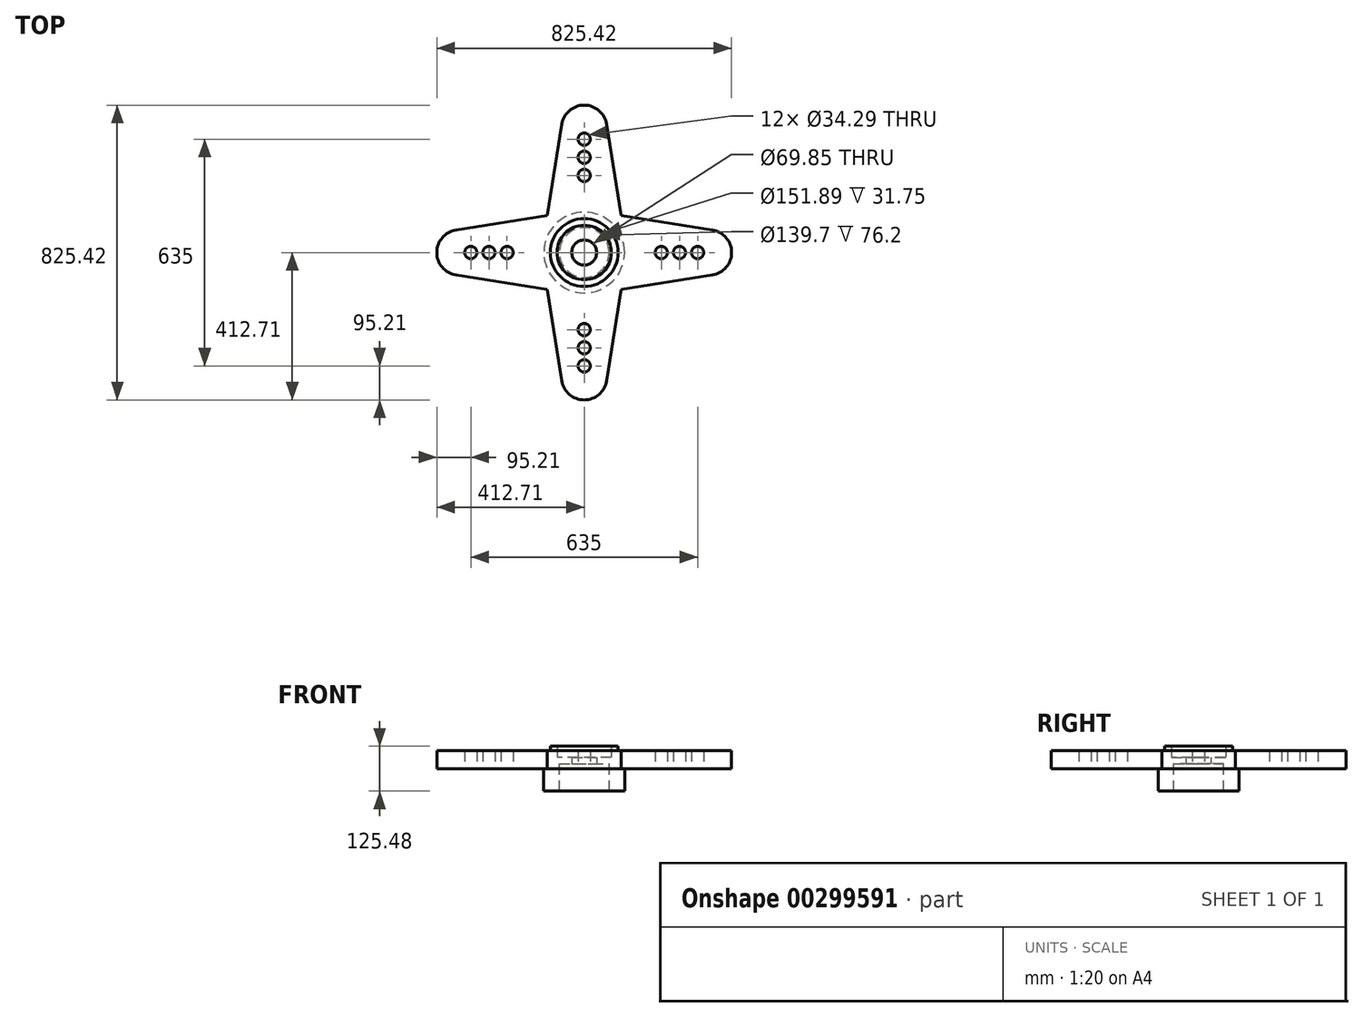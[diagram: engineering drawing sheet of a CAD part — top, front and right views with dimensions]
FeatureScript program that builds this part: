
annotation { "Feature Type Name" : "Feature", "Feature Type Description" : "" }
export const myFeature = defineFeature(function(context is Context, id is Id, definition is map)
    precondition{}
    {
        {
            var Q0;
            Q0=qCreatedBy(makeId("Top.planeOp"),FACE);
            var sketch = newSketch(context, id + "F0", { "sketchPlane" : qUnion([Q0])});
            skLineSegment(sketch, "E0", {"start": v(0, 0) * mm, "end": v(0, 635) * mm});
            skLineSegment(sketch, "E1", {"start": v(0, 0) * mm, "end": v(404.1, 404.1) * mm});
            skLineSegment(sketch, "E2", {"start": v(103.05, 103.05) * mm, "end": v(62.73, 359.1) * mm});
            skLineSegment(sketch, "E3", {"start": v(0, 412.71) * mm, "end": v(-177.36, 412.71) * mm});
            skArc(sketch, "E4", {"start": v(0, 412.71) * mm, "mid": v(41.26, 397.48) * mm, "end": v(62.73, 359.1) * mm});
            skCircle(sketch, "E5", {"center": v(0, 266.7) * mm, "radius": 17.15 * mm});
            skCircle(sketch, "E6", {"center": v(0, 317.5) * mm, "radius": 17.15 * mm});
            skCircle(sketch, "E7", {"center": v(0, 215.9) * mm, "radius": 17.15 * mm});
            skCircle(sketch, "E8", {"center": v(0, 0) * mm, "radius": 34.93 * mm});
            skLineSegment(sketch, "E9.MirrorCS", {"start": v(103.05, 103.05) * mm, "end": v(359.1, 62.73) * mm});
            skArc(sketch, "E10.MirrorCS", {"start": v(412.71, 0) * mm, "mid": v(397.48, 41.26) * mm, "end": v(359.1, 62.73) * mm});
            skCircle(sketch, "E11.MirrorC", {"center": v(215.9, 0) * mm, "radius": 17.15 * mm});
            skCircle(sketch, "E12.MirrorC", {"center": v(317.5, 0) * mm, "radius": 17.15 * mm});
            skCircle(sketch, "E13.MirrorC", {"center": v(266.7, 0) * mm, "radius": 17.15 * mm});
            skArc(sketch, "E14.MirrorCS", {"start": v(0, 412.71) * mm, "mid": v(-41.26, 397.48) * mm, "end": v(-62.73, 359.1) * mm});
            skLineSegment(sketch, "E15.MirrorCS", {"start": v(-103.05, 103.05) * mm, "end": v(-62.73, 359.1) * mm});
            skLineSegment(sketch, "E16.MirrorCS", {"start": v(-103.05, 103.05) * mm, "end": v(-359.1, 62.73) * mm});
            skArc(sketch, "E17.MirrorCS", {"start": v(-412.71, 0) * mm, "mid": v(-397.48, 41.26) * mm, "end": v(-359.1, 62.73) * mm});
            skCircle(sketch, "E18.MirrorC", {"center": v(-317.5, 0) * mm, "radius": 17.15 * mm});
            skCircle(sketch, "E19.MirrorC", {"center": v(-266.7, 0) * mm, "radius": 17.15 * mm});
            skCircle(sketch, "E20.MirrorC", {"center": v(-215.9, 0) * mm, "radius": 17.15 * mm});
            skLineSegment(sketch, "E21", {"start": v(0, 0) * mm, "end": v(710.63, 0) * mm});
            skArc(sketch, "E22.MirrorCS", {"start": v(-412.71, 0) * mm, "mid": v(-397.48, -41.26) * mm, "end": v(-359.1, -62.73) * mm});
            skLineSegment(sketch, "E23.MirrorCS", {"start": v(-103.05, -103.05) * mm, "end": v(-359.1, -62.73) * mm});
            skLineSegment(sketch, "E24.MirrorCS", {"start": v(-103.05, -103.05) * mm, "end": v(-62.73, -359.1) * mm});
            skArc(sketch, "E25.MirrorCS", {"start": v(0, -412.71) * mm, "mid": v(-41.26, -397.48) * mm, "end": v(-62.73, -359.1) * mm});
            skArc(sketch, "E26.MirrorCS", {"start": v(0, -412.71) * mm, "mid": v(41.26, -397.48) * mm, "end": v(62.73, -359.1) * mm});
            skLineSegment(sketch, "E27.MirrorCS", {"start": v(103.05, -103.05) * mm, "end": v(62.73, -359.1) * mm});
            skLineSegment(sketch, "E28.MirrorCS", {"start": v(103.05, -103.05) * mm, "end": v(359.1, -62.73) * mm});
            skArc(sketch, "E29.MirrorCS", {"start": v(412.71, 0) * mm, "mid": v(397.48, -41.26) * mm, "end": v(359.1, -62.73) * mm});
            skCircle(sketch, "E30.MirrorC", {"center": v(0, -215.9) * mm, "radius": 17.15 * mm});
            skCircle(sketch, "E31.MirrorC", {"center": v(0, -266.7) * mm, "radius": 17.15 * mm});
            skCircle(sketch, "E32.MirrorC", {"center": v(0, -317.5) * mm, "radius": 17.15 * mm});
            skSolve(sketch);
        }
        {
            var Q0;
            Q0 = qSketchRegion(id + "F0", true);
            extrude(context, id + "F1", {"entities" : qUnion([Q0]), "depth" : 50.8 * mm});
        }
        {
            var Q0;
            Q0=makeQuery(id+"F1.opExtrude","CAP_FACE",FACE,{"disambiguationData":[OSD([sQuery(id+"F0.wireOp",EDGE,"E2"),sQuery(id+"F0.wireOp",EDGE,"E4"),sQuery(id+"F0.wireOp",EDGE,"E5"),sQuery(id+"F0.wireOp",EDGE,"E6"),sQuery(id+"F0.wireOp",EDGE,"E7"),sQuery(id+"F0.wireOp",EDGE,"E8"),sQuery(id+"F0.wireOp",EDGE,"E9.MirrorCS"),sQuery(id+"F0.wireOp",EDGE,"E10.MirrorCS"),sQuery(id+"F0.wireOp",EDGE,"E11.MirrorC"),sQuery(id+"F0.wireOp",EDGE,"E12.MirrorC"),sQuery(id+"F0.wireOp",EDGE,"E13.MirrorC"),sQuery(id+"F0.wireOp",EDGE,"E14.MirrorCS"),sQuery(id+"F0.wireOp",EDGE,"E15.MirrorCS"),sQuery(id+"F0.wireOp",EDGE,"E16.MirrorCS"),sQuery(id+"F0.wireOp",EDGE,"E17.MirrorCS"),sQuery(id+"F0.wireOp",EDGE,"E18.MirrorC"),sQuery(id+"F0.wireOp",EDGE,"E19.MirrorC"),sQuery(id+"F0.wireOp",EDGE,"E20.MirrorC"),sQuery(id+"F0.wireOp",EDGE,"E22.MirrorCS"),sQuery(id+"F0.wireOp",EDGE,"E23.MirrorCS"),sQuery(id+"F0.wireOp",EDGE,"E24.MirrorCS"),sQuery(id+"F0.wireOp",EDGE,"E25.MirrorCS"),sQuery(id+"F0.wireOp",EDGE,"E26.MirrorCS"),sQuery(id+"F0.wireOp",EDGE,"E27.MirrorCS"),sQuery(id+"F0.wireOp",EDGE,"E28.MirrorCS"),sQuery(id+"F0.wireOp",EDGE,"E29.MirrorCS"),sQuery(id+"F0.wireOp",EDGE,"E30.MirrorC"),sQuery(id+"F0.wireOp",EDGE,"E31.MirrorC"),sQuery(id+"F0.wireOp",EDGE,"E32.MirrorC")])],"isStart":false});
            var sketch = newSketch(context, id + "F2", { "sketchPlane" : qUnion([Q0])});
            skCircle(sketch, "E33", {"center": v(0, 0) * mm, "radius": 75.95 * mm});
            skCircle(sketch, "E34", {"center": v(0, 0) * mm, "radius": 95 * mm});
            skSolve(sketch);
        }
        {
            var Q0;
            Q0 = qSketchRegion(id + "F2", true);
            extrude(context, id + "F3", {"entities" : qUnion([Q0]), "operationType" : NewBodyOperationType.ADD, "depth" : 12.7 * mm});
        }
        {
            var Q0;
            Q0=makeQuery(id+"F3.opExtrude","CAP_FACE",FACE,{"disambiguationData":[OSD([sQuery(id+"F2.wireOp",EDGE,"E33"),sQuery(id+"F2.wireOp",EDGE,"E34")])],"isStart":false});
            var sketch = newSketch(context, id + "F4", { "sketchPlane" : qUnion([Q0])});
            skCircle(sketch, "E35", {"center": v(0, 0) * mm, "radius": 75.95 * mm});
            skSolve(sketch);
        }
        {
            var Q0;
            Q0 = qSketchRegion(id + "F4", true);
            extrude(context, id + "F5", {"entities" : qUnion([Q0]), "operationType" : NewBodyOperationType.REMOVE, "oppositeDirection" : true, "depth" : 31.75 * mm});
        }
        {
            var Q0;
            Q0=makeQuery(id+"F1.opExtrude","CAP_FACE",FACE,{"disambiguationData":[OSD([sQuery(id+"F0.wireOp",EDGE,"E2"),sQuery(id+"F0.wireOp",EDGE,"E4"),sQuery(id+"F0.wireOp",EDGE,"E5"),sQuery(id+"F0.wireOp",EDGE,"E6"),sQuery(id+"F0.wireOp",EDGE,"E7"),sQuery(id+"F0.wireOp",EDGE,"E8"),sQuery(id+"F0.wireOp",EDGE,"E9.MirrorCS"),sQuery(id+"F0.wireOp",EDGE,"E10.MirrorCS"),sQuery(id+"F0.wireOp",EDGE,"E11.MirrorC"),sQuery(id+"F0.wireOp",EDGE,"E12.MirrorC"),sQuery(id+"F0.wireOp",EDGE,"E13.MirrorC"),sQuery(id+"F0.wireOp",EDGE,"E14.MirrorCS"),sQuery(id+"F0.wireOp",EDGE,"E15.MirrorCS"),sQuery(id+"F0.wireOp",EDGE,"E16.MirrorCS"),sQuery(id+"F0.wireOp",EDGE,"E17.MirrorCS"),sQuery(id+"F0.wireOp",EDGE,"E18.MirrorC"),sQuery(id+"F0.wireOp",EDGE,"E19.MirrorC"),sQuery(id+"F0.wireOp",EDGE,"E20.MirrorC"),sQuery(id+"F0.wireOp",EDGE,"E22.MirrorCS"),sQuery(id+"F0.wireOp",EDGE,"E23.MirrorCS"),sQuery(id+"F0.wireOp",EDGE,"E24.MirrorCS"),sQuery(id+"F0.wireOp",EDGE,"E25.MirrorCS"),sQuery(id+"F0.wireOp",EDGE,"E26.MirrorCS"),sQuery(id+"F0.wireOp",EDGE,"E27.MirrorCS"),sQuery(id+"F0.wireOp",EDGE,"E28.MirrorCS"),sQuery(id+"F0.wireOp",EDGE,"E29.MirrorCS"),sQuery(id+"F0.wireOp",EDGE,"E30.MirrorC"),sQuery(id+"F0.wireOp",EDGE,"E31.MirrorC"),sQuery(id+"F0.wireOp",EDGE,"E32.MirrorC")])],"isStart":true});
            var sketch = newSketch(context, id + "F6", { "sketchPlane" : qUnion([Q0])});
            skCircle(sketch, "E36", {"center": v(0, 0) * mm, "radius": 113.03 * mm});
            skCircle(sketch, "E37", {"center": v(0, 0) * mm, "radius": 69.85 * mm});
            skSolve(sketch);
        }
        {
            var Q0;
            Q0 = qSketchRegion(id + "F6", true);
            extrude(context, id + "F7", {"entities" : qUnion([Q0]), "operationType" : NewBodyOperationType.ADD, "depth" : 61.98 * mm});
        }
        {
            var Q0;
            Q0=makeQuery(id+"F7.opExtrude","CAP_FACE",FACE,{"disambiguationData":[OSD([sQuery(id+"F6.wireOp",EDGE,"E36"),sQuery(id+"F6.wireOp",EDGE,"E37")])],"isStart":false});
            var sketch = newSketch(context, id + "F8", { "sketchPlane" : qUnion([Q0])});
            skCircle(sketch, "E38", {"center": v(0, 0) * mm, "radius": 69.85 * mm});
            skSolve(sketch);
        }
        {
            var Q0;
            Q0 = qSketchRegion(id + "F8", true);
            extrude(context, id + "F9", {"entities" : qUnion([Q0]), "operationType" : NewBodyOperationType.REMOVE, "oppositeDirection" : true, "depth" : 76.2 * mm});
        }
    });
